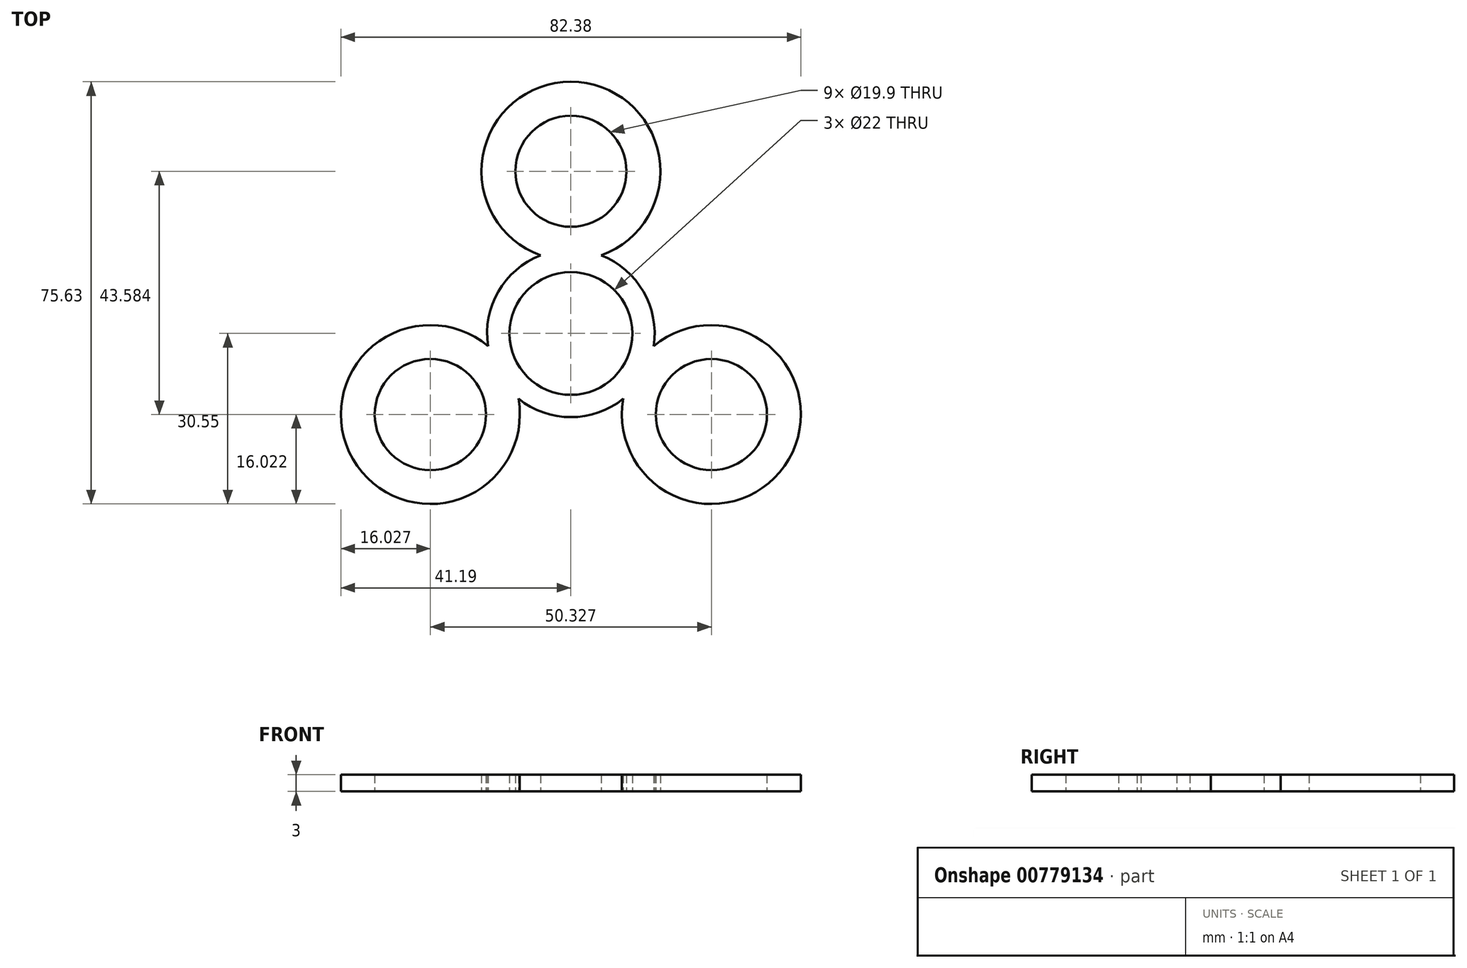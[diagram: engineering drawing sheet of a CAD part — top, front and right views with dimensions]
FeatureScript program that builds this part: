
annotation { "Feature Type Name" : "Feature", "Feature Type Description" : "" }
export const myFeature = defineFeature(function(context is Context, id is Id, definition is map)
    precondition{}
    {
        {
            var Q0;
            Q0=qCreatedBy(makeId("Top.planeOp"),FACE);
            var sketch = newSketch(context, id + "F0", { "sketchPlane" : qUnion([Q0])});
            skArc(sketch, "E0", {"start": v(9.53, 5.5) * mm, "mid": v(0, 11) * mm, "end": v(-9.53, 5.5) * mm});
            skArc(sketch, "E1", {"start": v(13, 7.5) * mm, "mid": v(9.77, 11.39) * mm, "end": v(5.43, 13.98) * mm});
            skArc(sketch, "E2", {"start": v(5.43, 13.98) * mm, "mid": v(0, 45.08) * mm, "end": v(-5.43, 13.98) * mm});
            skCircle(sketch, "E3", {"center": v(0, 29.06) * mm, "radius": 9.95 * mm});
            skArc(sketch, "E4.trimOffspring", {"start": v(-5.43, 13.98) * mm, "mid": v(-9.77, 11.39) * mm, "end": v(-13, 7.5) * mm});
            skCircle(sketch, "E5.1.0", {"center": v(-25.16, -14.53) * mm, "radius": 9.95 * mm});
            skArc(sketch, "E5.1.1", {"start": v(-14.83, -2.28) * mm, "mid": v(-39.04, -22.54) * mm, "end": v(-9.4, -11.7) * mm});
            skArc(sketch, "E5.1.2", {"start": v(-13, 7.5) * mm, "mid": v(-14.74, 2.76) * mm, "end": v(-14.83, -2.28) * mm});
            skArc(sketch, "E5.1.3", {"start": v(-9.53, 5.5) * mm, "mid": v(-9.53, -5.5) * mm, "end": v(0, -11) * mm});
            skArc(sketch, "E5.1.4", {"start": v(-9.4, -11.7) * mm, "mid": v(-4.98, -14.15) * mm, "end": v(0, -15) * mm});
            skCircle(sketch, "E5.2.0", {"center": v(25.16, -14.53) * mm, "radius": 9.95 * mm});
            skArc(sketch, "E5.2.1", {"start": v(9.4, -11.7) * mm, "mid": v(39.04, -22.54) * mm, "end": v(14.83, -2.28) * mm});
            skArc(sketch, "E5.2.2", {"start": v(0, -15) * mm, "mid": v(4.98, -14.15) * mm, "end": v(9.4, -11.7) * mm});
            skArc(sketch, "E5.2.3", {"start": v(0, -11) * mm, "mid": v(9.53, -5.5) * mm, "end": v(9.53, 5.5) * mm});
            skArc(sketch, "E5.2.4", {"start": v(14.83, -2.28) * mm, "mid": v(14.74, 2.76) * mm, "end": v(13, 7.5) * mm});
            skSolve(sketch);
        }
        {
            var Q0;
            Q0 = qSketchRegion(id + "F0", true);
            extrude(context, id + "F1", {"entities" : qUnion([Q0]), "depth" : 3 * mm, "offsetDistance" : 25 * mm});
        }
    });
